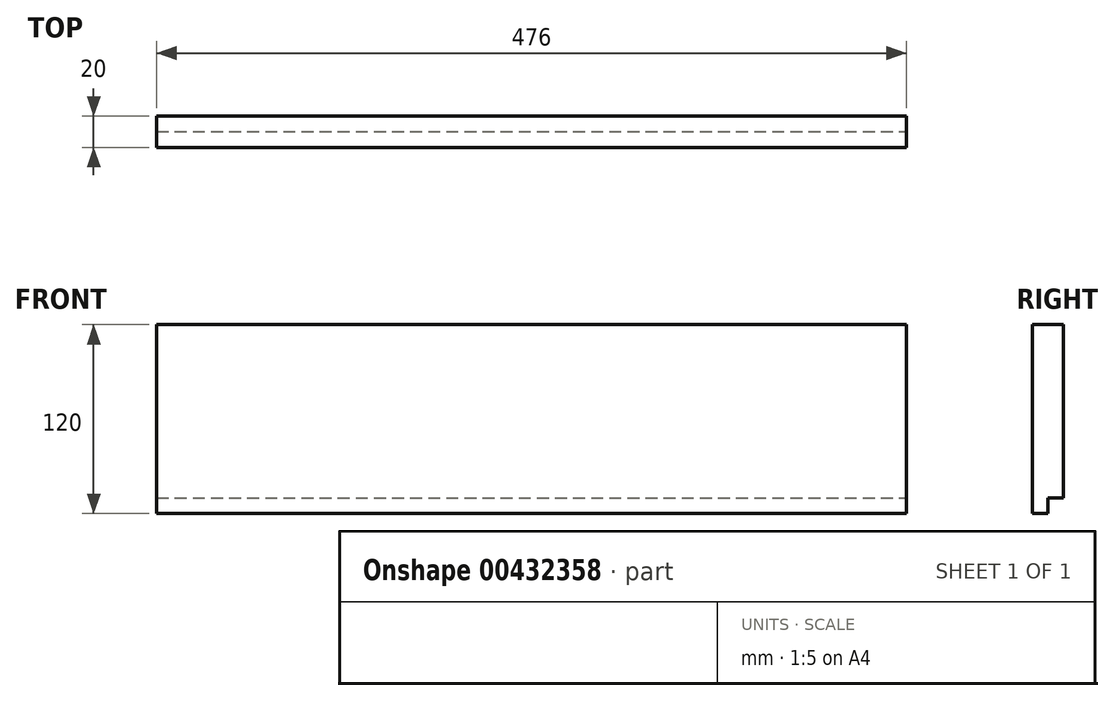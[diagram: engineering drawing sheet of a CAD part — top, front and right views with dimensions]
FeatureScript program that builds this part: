
annotation { "Feature Type Name" : "Feature", "Feature Type Description" : "" }
export const myFeature = defineFeature(function(context is Context, id is Id, definition is map)
    precondition{}
    {
        {
            var Q0;
            Q0=qCreatedBy(makeId("Front.planeOp"),FACE);
            var sketch = newSketch(context, id + "F0", { "sketchPlane" : qUnion([Q0])});
            skLineSegment(sketch, "E0.bottom", {"start": v(-238, 60) * mm, "end": v(238, 60) * mm});
            skLineSegment(sketch, "E0.top", {"start": v(-238, -60) * mm, "end": v(238, -60) * mm});
            skLineSegment(sketch, "E0.left", {"start": v(-238, 60) * mm, "end": v(-238, -60) * mm});
            skLineSegment(sketch, "E0.right", {"start": v(238, 60) * mm, "end": v(238, -60) * mm});
            skPoint(sketch, "E0.middle", {"position": v(0, 0) * mm});
            skLineSegment(sketch, "E1", {"start": v(-238, -50) * mm, "end": v(238, -50) * mm});
            skSolve(sketch);
        }
        {
            var Q0;
            {var subQ0=sQuery(id+"F0.wireOp",EDGE,"E0.top");Q0=makeQuery(id+"F0.imprint","IMPRINT",FACE,{"disambiguationData":[TD([[makeQuery(id+"F0.imprint","IMPRINT",EDGE,{"derivedFrom":subQ0}),1.0]])]});}
            extrude(context, id + "F1", {"entities" : qUnion([Q0]), "depth" : 10 * mm});
        }
        {
            var Q0;
            {var subQ0=sQuery(id+"F0.wireOp",EDGE,"E0.bottom");Q0=makeQuery(id+"F0.imprint","IMPRINT",FACE,{"disambiguationData":[TD([[makeQuery(id+"F0.imprint","IMPRINT",EDGE,{"derivedFrom":subQ0}),-1.0]])]});}
            extrude(context, id + "F2", {"entities" : qUnion([Q0]), "operationType" : NewBodyOperationType.ADD, "endBound" : BoundingType.SYMMETRIC, "depth" : 20 * mm});
        }
    });
